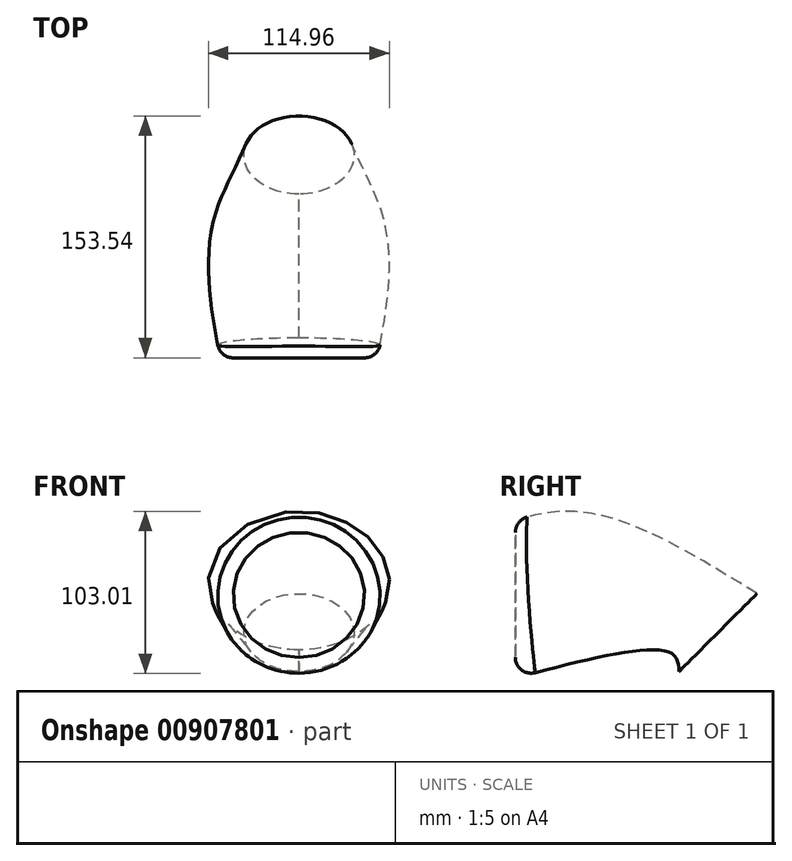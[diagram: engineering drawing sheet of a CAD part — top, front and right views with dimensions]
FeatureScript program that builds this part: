
annotation { "Feature Type Name" : "Feature", "Feature Type Description" : "" }
export const myFeature = defineFeature(function(context is Context, id is Id, definition is map)
    precondition{}
    {
        {
            var Q0;
            Q0=qCreatedBy(makeId("Front.planeOp"),FACE);
            cPlane(context, id + "F0", {"entities" : qUnion([Q0]), "cplaneType" : CPlaneType.OFFSET, "offset" : 100 * mm, "width" : 150 * mm, "height" : 150 * mm});
        }
        {
            var Q0;
            Q0=qCreatedBy(makeId("Front.planeOp"),FACE);
            cPlane(context, id + "F1", {"entities" : qUnion([Q0]), "cplaneType" : CPlaneType.OFFSET, "offset" : 50 * mm, "oppositeDirection" : true, "width" : 150 * mm, "height" : 150 * mm});
        }
        {
            var Q0;
            Q0=qCreatedBy(id+"F1.planeOp",FACE);
            var sketch = newSketch(context, id + "F2", { "sketchPlane" : qUnion([Q0])});
            skLineSegment(sketch, "E0", {"start": v(-75, 0) * mm, "end": v(75, 0) * mm});
            skSolve(sketch);
        }
        {
            var Q0;
            Q0=qCreatedBy(id+"F1.planeOp",FACE);
            var Q1;
            Q1=sQuery(id+"F2.wireOp",EDGE,"E0");
            cPlane(context, id + "F3", {"entities" : qUnion([Q0, Q1]), "cplaneType" : CPlaneType.LINE_ANGLE, "offset" : 25 * mm, "angle" : 45 * degree, "oppositeDirection" : true, "width" : 150 * mm, "height" : 150 * mm});
        }
        {
            var Q0;
            Q0=qCreatedBy(id+"F0.planeOp",FACE);
            var sketch = newSketch(context, id + "F4", { "sketchPlane" : qUnion([Q0])});
            skCircle(sketch, "E1", {"center": v(0, 0) * mm, "radius": 50 * mm});
            skSolve(sketch);
        }
        {
            var Q0;
            Q0=qCreatedBy(makeId("Front.planeOp"),FACE);
            var sketch = newSketch(context, id + "F5", { "sketchPlane" : qUnion([Q0])});
            skPoint(sketch, "E2", {"position": v(50, 0) * mm});
            skPoint(sketch, "E3", {"position": v(0, 35) * mm});
            skEllipse(sketch, "E4", {"center": v(0, 0) * mm, "majorRadius": 50 * mm, "minorRadius": 35 * mm, "majorAxis": v(1, 0)});
            skSolve(sketch);
        }
        {
            var Q0;
            Q0=qCreatedBy(id+"F3.planeOp",FACE);
            var sketch = newSketch(context, id + "F6", { "sketchPlane" : qUnion([Q0])});
            skPoint(sketch, "E5", {"position": v(0, 5.36) * mm});
            skCircle(sketch, "E6", {"center": v(0, 5.36) * mm, "radius": 35 * mm});
            skSolve(sketch);
        }
        {
            var Q0;
            Q0=makeQuery(id+"F4.imprint","IMPRINT",FACE,{"disambiguationData":[TD([[makeQuery(id+"F4.imprint","IMPRINT",EDGE,{"derivedFrom":sQuery(id+"F4.wireOp",EDGE,"E1")}),1.0]])]});
            var Q1;
            Q1=makeQuery(id+"F5.imprint","IMPRINT",FACE,{"disambiguationData":[TD([[makeQuery(id+"F5.imprint","IMPRINT",EDGE,{"derivedFrom":sQuery(id+"F5.wireOp",EDGE,"E4")}),1.0]])]});
            var Q2;
            Q2=makeQuery(id+"F6.imprint","IMPRINT",FACE,{"disambiguationData":[TD([[makeQuery(id+"F6.imprint","IMPRINT",EDGE,{"derivedFrom":sQuery(id+"F6.wireOp",EDGE,"E6")}),1.0]])]});
            loft(context, id + "F7", {"sheetProfilesArray" : [{ "sheetProfileEntities" : qUnion([Q0]) }, { "sheetProfileEntities" : qUnion([Q1]) }, { "sheetProfileEntities" : qUnion([Q2]) }]});
        }
        {
            var Q0;
            Q0=makeQuery(id+"F7.opLoft","MID_CAP_EDGE",EDGE,{"disambiguationData":[OSD([sQuery(id+"F4.wireOp",EDGE,"E1")])],"capPos":0.0});
            fillet(context, id + "F8", {"entities" : qUnion([Q0]), "radius" : 10 * mm, "tangentPropagation" : true, "allowEdgeOverflow" : false});
        }
    });
